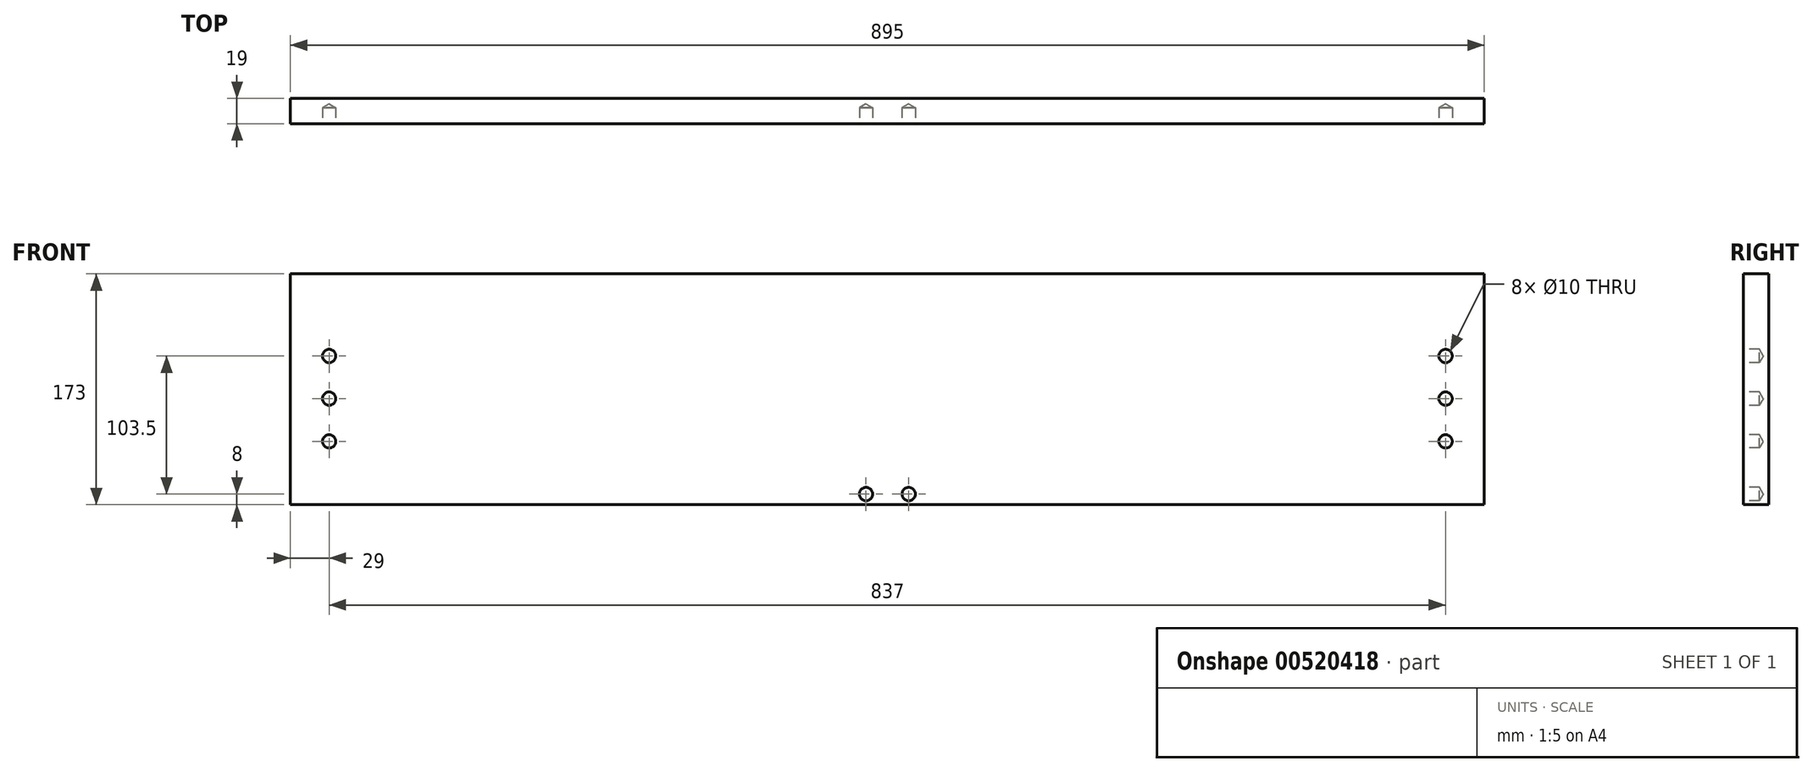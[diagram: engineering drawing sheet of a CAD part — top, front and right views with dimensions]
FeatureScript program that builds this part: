
annotation { "Feature Type Name" : "Feature", "Feature Type Description" : "" }
export const myFeature = defineFeature(function(context is Context, id is Id, definition is map)
    precondition{}
    {
        {
            var Q0;
            Q0=qCreatedBy(makeId("Right.planeOp"),FACE);
            var sketch = newSketch(context, id + "F0", { "sketchPlane" : qUnion([Q0])});
            skLineSegment(sketch, "E0.bottom", {"start": v(0, 0) * mm, "end": v(-19, 0) * mm});
            skLineSegment(sketch, "E0.top", {"start": v(0, 173) * mm, "end": v(-19, 173) * mm});
            skLineSegment(sketch, "E0.left", {"start": v(0, 0) * mm, "end": v(0, 173) * mm});
            skLineSegment(sketch, "E0.right", {"start": v(-19, 0) * mm, "end": v(-19, 173) * mm});
            skSolve(sketch);
        }
        {
            var Q0;
            Q0=makeQuery(id+"F0.imprint","IMPRINT",FACE,{"disambiguationData":[TD([[makeQuery(id+"F0.imprint","IMPRINT",EDGE,{"derivedFrom":sQuery(id+"F0.wireOp",EDGE,"E0.bottom")}),-1.0]])]});
            extrude(context, id + "F1", {"entities" : qUnion([Q0]), "depth" : 895 * mm, "offsetDistance" : 25 * mm});
        }
        {
            var Q0;
            Q0=makeQuery(id+"F1.opExtrude","SWEPT_FACE",FACE,{"disambiguationData":[OSD([sQuery(id+"F0.wireOp",EDGE,"E0.right")])]});
            var sketch = newSketch(context, id + "F2", { "sketchPlane" : qUnion([Q0])});
            skLineSegment(sketch, "E1", {"start": v(447.5, 173) * mm, "end": v(447.5, 0) * mm, "construction": true});
            skLineSegment(sketch, "E2", {"start": v(13.5, 116) * mm, "end": v(13.5, 0) * mm, "construction": true});
            skLineSegment(sketch, "E3", {"start": v(13.5, 0) * mm, "end": v(29, 0) * mm, "construction": true});
            skLineSegment(sketch, "E4", {"start": v(29, 0) * mm, "end": v(29, 111.5) * mm, "construction": true});
            skPoint(sketch, "E5", {"position": v(29, 111.5) * mm});
            skPoint(sketch, "E6", {"position": v(29, 79.5) * mm});
            skPoint(sketch, "E7", {"position": v(29, 47.5) * mm});
            skPoint(sketch, "E8", {"position": v(431.5, 8) * mm});
            skLineSegment(sketch, "E9", {"start": v(29, 8) * mm, "end": v(447.5, 8) * mm, "construction": true});
            skPoint(sketch, "E10.MirrorP", {"position": v(463.5, 8) * mm});
            skPoint(sketch, "E11.MirrorP", {"position": v(866, 47.5) * mm});
            skPoint(sketch, "E12.MirrorP", {"position": v(866, 79.5) * mm});
            skPoint(sketch, "E13.MirrorP", {"position": v(866, 111.5) * mm});
            skSolve(sketch);
        }
        {
            var Q0;
            Q0=sQuery(id+"F2.wireOp",VERTEX,"E5");
            var Q1;
            Q1=sQuery(id+"F2.wireOp",VERTEX,"E6");
            var Q2;
            Q2=sQuery(id+"F2.wireOp",VERTEX,"E7");
            var Q3;
            Q3=sQuery(id+"F2.wireOp",VERTEX,"E8");
            var Q4;
            Q4=sQuery(id+"F2.wireOp",VERTEX,"E10.MirrorP");
            var Q5;
            Q5=sQuery(id+"F2.wireOp",VERTEX,"E11.MirrorP");
            var Q6;
            Q6=sQuery(id+"F2.wireOp",VERTEX,"E12.MirrorP");
            var Q7;
            Q7=sQuery(id+"F2.wireOp",VERTEX,"E13.MirrorP");
            var Q8;
            Q8=makeQuery(id+"F1.opExtrude","SWEPT_BODY",BODY,{"disambiguationData":[OSD([sQuery(id+"F0.wireOp",EDGE,"E0.bottom"),sQuery(id+"F0.wireOp",EDGE,"E0.top"),sQuery(id+"F0.wireOp",EDGE,"E0.left"),sQuery(id+"F0.wireOp",EDGE,"E0.right")])]});
            hole(context, id + "F3", {"style" : HoleStyle.SIMPLE, "endStyle" : HoleEndStyle.BLIND, "holeDiameter" : 10 * mm, "majorDiameter" : 5 * mm, "holeDepth" : 12 * mm, "isTappedThrough" : true, "tappedDepth" : 12 * mm, "tapClearance" : 3, "startFromSketch" : true, "locations" : qUnion([Q0, Q1, Q2, Q3, Q4, Q5, Q6, Q7]), "scope" : qUnion([Q8])});
        }
    });
